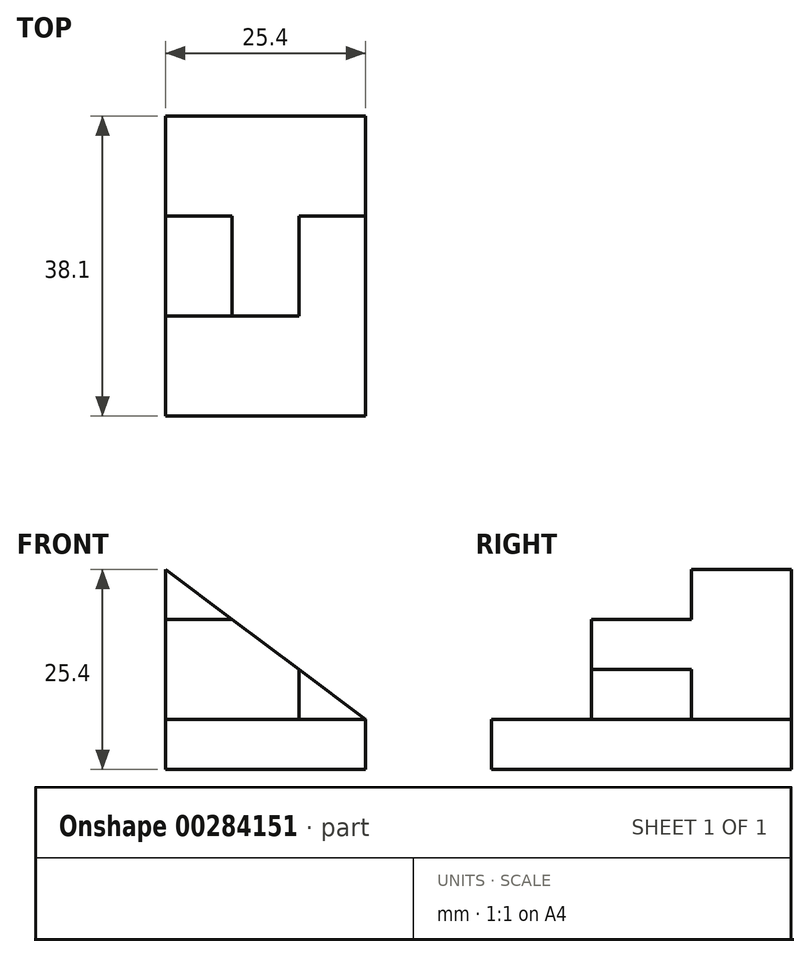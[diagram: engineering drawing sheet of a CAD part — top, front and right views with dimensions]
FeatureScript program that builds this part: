
annotation { "Feature Type Name" : "Feature", "Feature Type Description" : "" }
export const myFeature = defineFeature(function(context is Context, id is Id, definition is map)
    precondition{}
    {
        {
            var Q0;
            Q0=qCreatedBy(makeId("Front.planeOp"),FACE);
            var sketch = newSketch(context, id + "F0", { "sketchPlane" : qUnion([Q0])});
            skLineSegment(sketch, "E0", {"start": v(0, 0) * mm, "end": v(0, 25.4) * mm});
            skLineSegment(sketch, "E1", {"start": v(0, 25.4) * mm, "end": v(25.4, 6.35) * mm});
            skLineSegment(sketch, "E2", {"start": v(25.4, 6.35) * mm, "end": v(25.4, 0) * mm});
            skLineSegment(sketch, "E3", {"start": v(25.4, 0) * mm, "end": v(0, 0) * mm});
            skSolve(sketch);
        }
        {
            var Q0;
            Q0=makeQuery(id+"F0.imprint","IMPRINT",FACE,{"disambiguationData":[TD([[makeQuery(id+"F0.imprint","IMPRINT",EDGE,{"derivedFrom":sQuery(id+"F0.wireOp",EDGE,"E0")}),-1.0]])]});
            extrude(context, id + "F1", {"entities" : qUnion([Q0]), "depth" : 38.1 * mm});
        }
        {
            var Q0;
            Q0=makeQuery(id+"F1.opExtrude","CAP_FACE",FACE,{"disambiguationData":[OSD([sQuery(id+"F0.wireOp",EDGE,"E0"),sQuery(id+"F0.wireOp",EDGE,"E1"),sQuery(id+"F0.wireOp",EDGE,"E2"),sQuery(id+"F0.wireOp",EDGE,"E3")])],"isStart":false});
            var sketch = newSketch(context, id + "F2", { "sketchPlane" : qUnion([Q0])});
            skLineSegment(sketch, "E4", {"start": v(0, 25.4) * mm, "end": v(25.4, 6.35) * mm});
            skLineSegment(sketch, "E5", {"start": v(25.4, 6.35) * mm, "end": v(0, 6.35) * mm});
            skLineSegment(sketch, "E6", {"start": v(0, 6.35) * mm, "end": v(0, 25.4) * mm});
            skSolve(sketch);
        }
        {
            var Q0;
            Q0 = qSketchRegion(id + "F2", true);
            extrude(context, id + "F3", {"entities" : qUnion([Q0]), "operationType" : NewBodyOperationType.REMOVE, "oppositeDirection" : true, "depth" : 12.7 * mm});
        }
        {
            var Q0;
            Q0=makeQuery(id+"F3.boolean.opBoolean","COPY",FACE,{"derivedFrom":makeQuery(id+"F3.opExtrude","CAP_FACE",FACE,{"disambiguationData":[OSD([sQuery(id+"F2.wireOp",EDGE,"E4"),sQuery(id+"F2.wireOp",EDGE,"E5"),sQuery(id+"F2.wireOp",EDGE,"E6")])],"isStart":false})});
            var sketch = newSketch(context, id + "F4", { "sketchPlane" : qUnion([Q0])});
            skLineSegment(sketch, "E7", {"start": v(0, 25.4) * mm, "end": v(0, 19.05) * mm});
            skLineSegment(sketch, "E8", {"start": v(0, 19.05) * mm, "end": v(8.47, 19.05) * mm});
            skLineSegment(sketch, "E9", {"start": v(8.47, 19.05) * mm, "end": v(0, 25.4) * mm});
            skSolve(sketch);
        }
        {
            var Q0;
            Q0=makeQuery(id+"F4.imprint","IMPRINT",FACE,{"disambiguationData":[TD([[makeQuery(id+"F4.imprint","IMPRINT",EDGE,{"derivedFrom":sQuery(id+"F4.wireOp",EDGE,"E7")}),-1.0]])]});
            extrude(context, id + "F5", {"entities" : qUnion([Q0]), "operationType" : NewBodyOperationType.REMOVE, "oppositeDirection" : true, "depth" : 12.7 * mm});
        }
        {
            var Q0;
            Q0=makeQuery(id+"F3.boolean.opBoolean","COPY",FACE,{"derivedFrom":makeQuery(id+"F3.opExtrude","CAP_FACE",FACE,{"disambiguationData":[OSD([sQuery(id+"F2.wireOp",EDGE,"E4"),sQuery(id+"F2.wireOp",EDGE,"E5"),sQuery(id+"F2.wireOp",EDGE,"E6")])],"isStart":false})});
            var sketch = newSketch(context, id + "F6", { "sketchPlane" : qUnion([Q0])});
            skLineSegment(sketch, "E10", {"start": v(25.4, 6.35) * mm, "end": v(16.93, 6.35) * mm});
            skLineSegment(sketch, "E11", {"start": v(16.93, 6.35) * mm, "end": v(16.93, 12.7) * mm});
            skLineSegment(sketch, "E12", {"start": v(16.93, 12.7) * mm, "end": v(25.4, 6.35) * mm});
            skSolve(sketch);
        }
        {
            var Q0;
            Q0=makeQuery(id+"F6.imprint","IMPRINT",FACE,{"disambiguationData":[TD([[makeQuery(id+"F6.imprint","IMPRINT",EDGE,{"derivedFrom":sQuery(id+"F6.wireOp",EDGE,"E10")}),-1.0]])]});
            extrude(context, id + "F7", {"entities" : qUnion([Q0]), "operationType" : NewBodyOperationType.REMOVE, "oppositeDirection" : true, "depth" : 12.7 * mm});
        }
    });
